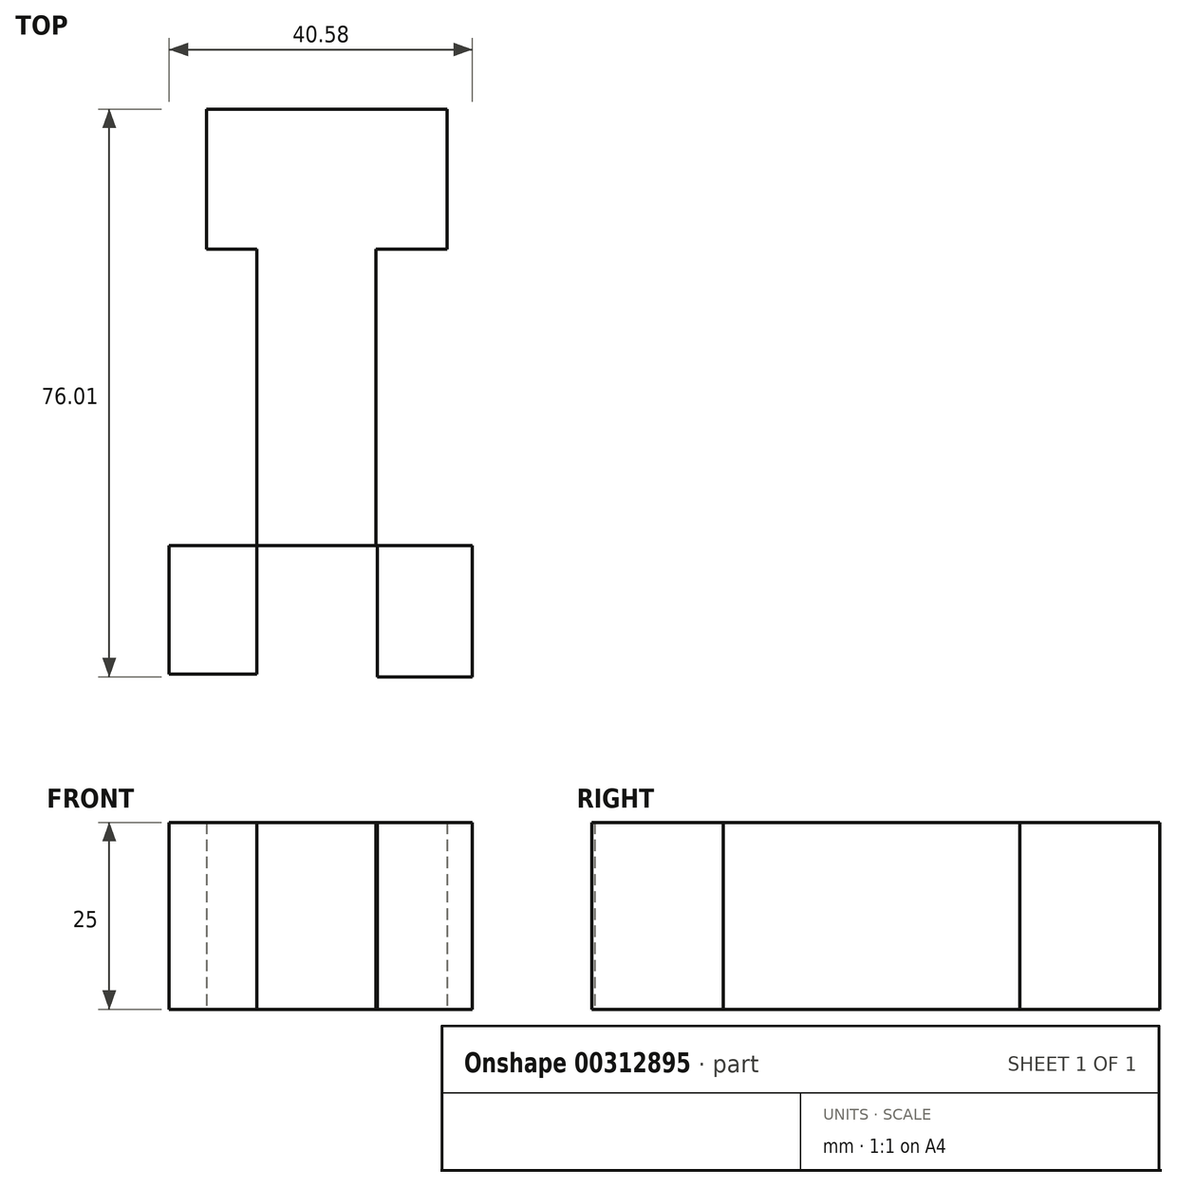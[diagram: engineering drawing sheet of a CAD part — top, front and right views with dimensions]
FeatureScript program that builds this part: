
annotation { "Feature Type Name" : "Feature", "Feature Type Description" : "" }
export const myFeature = defineFeature(function(context is Context, id is Id, definition is map)
    precondition{}
    {
        {
            var Q0;
            Q0=qCreatedBy(makeId("Top.planeOp"),FACE);
            var sketch = newSketch(context, id + "F0", { "sketchPlane" : qUnion([Q0])});
            skLineSegment(sketch, "E0.bottom", {"start": v(0, 0) * mm, "end": v(-11.76, 0) * mm});
            skLineSegment(sketch, "E0.top", {"start": v(0, -17.24) * mm, "end": v(-11.76, -17.24) * mm});
            skLineSegment(sketch, "E0.left", {"start": v(0, 0) * mm, "end": v(0, -17.24) * mm});
            skLineSegment(sketch, "E0.right", {"start": v(-11.76, 0) * mm, "end": v(-11.76, -17.24) * mm});
            skLineSegment(sketch, "E1.bottom", {"start": v(16.1, 0) * mm, "end": v(28.82, 0) * mm});
            skLineSegment(sketch, "E1.top", {"start": v(16.1, -17.59) * mm, "end": v(28.82, -17.59) * mm});
            skLineSegment(sketch, "E1.left", {"start": v(16.1, 0) * mm, "end": v(16.1, -17.59) * mm});
            skLineSegment(sketch, "E1.right", {"start": v(28.82, 0) * mm, "end": v(28.82, -17.59) * mm});
            skLineSegment(sketch, "E2.bottom", {"start": v(0, 0) * mm, "end": v(15.9, 0) * mm});
            skLineSegment(sketch, "E2.top", {"start": v(0, 40.33) * mm, "end": v(15.9, 40.33) * mm});
            skLineSegment(sketch, "E2.left", {"start": v(0, 0) * mm, "end": v(0, 40.33) * mm});
            skLineSegment(sketch, "E2.right", {"start": v(15.9, 0) * mm, "end": v(15.9, 40.33) * mm});
            skLineSegment(sketch, "E3.bottom", {"start": v(-6.78, 58.42) * mm, "end": v(25.43, 58.42) * mm});
            skLineSegment(sketch, "E3.top", {"start": v(-6.78, 39.68) * mm, "end": v(25.43, 39.68) * mm});
            skLineSegment(sketch, "E3.left", {"start": v(-6.78, 58.42) * mm, "end": v(-6.78, 39.68) * mm});
            skLineSegment(sketch, "E3.right", {"start": v(25.43, 58.42) * mm, "end": v(25.43, 39.68) * mm});
            skSolve(sketch);
        }
        {
            var Q0;
            Q0 = qSketchRegion(id + "F0", true);
            extrude(context, id + "F1", {"entities" : qUnion([Q0]), "depth" : 25 * mm, "offsetDistance" : 25 * mm});
        }
    });
